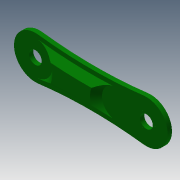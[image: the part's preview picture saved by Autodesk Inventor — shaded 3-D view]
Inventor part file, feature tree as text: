
AUTODESK INVENTOR PART (.ipt)
format: ipt  version: 2013 (Build 170138000, 138)  size: 299,008 bytes
history: native  units: mm
features: sketch x19, extrude x17, chamfer x1
ambient origin geometry x8: Origin, YZ Plane, XZ Plane, XY Plane, X Axis, Y Axis, Z Axis, Center Point
bodies: Solid1 (feature_tree)
feature tree (37):
  extrude  "Extrusion1"  Depth=50.0mm
  extrude  "Extrusion2"  Depth=6.0mm
  extrude  "Extrusion3"  Depth=5.0mm TaperAngle=0.0deg
  extrude  "Extrusion4"  Depth=20.0mm
  extrude  "Extrusion5"  Depth=20.0mm
  extrude  "Extrusion6"  Depth=3.0mm
  sketch  "Sketch7"  dims[d22=3.0mm d23=5.0mm d24=0.0mm]
  extrude  "Extrusion7"  Depth=5.0mm TaperAngle=0.0deg
  extrude  "Extrusion8"  Depth=1.0mm
  extrude  "Extrusion9"  Depth=1.0mm
  extrude  "Extrusion10"  Depth=15.0mm
  extrude  "Extrusion11"  Depth=5.0mm TaperAngle=0.0deg
  sketch  "Sketch12"  dims[d44=1.0mm d45=1.0mm]
  sketch  "Sketch13"  dims[d46=1.0mm d47=5.0mm d48=0.0mm]
  extrude  "Extrusion12"  Depth=1.0mm
  extrude  "Extrusion13"  Depth=5.0mm TaperAngle=0.0deg
  extrude  "Extrusion14"  Depth=5.0mm TaperAngle=0.0deg
  extrude  "Extrusion15"  Depth=5.0mm TaperAngle=0.0deg
  extrude  "Extrusion16"  Depth=43.308mm
  sketch  "Sketch18"  dims[d62=33.15mm]
  extrude  "Extrusion17"  Depth=20.0mm
  chamfer  "Chamfer1"  Distance=5.0mm
  sketch  "Sketch1"  dims[d0=150.0mm d1=50.0mm]
  sketch  "Sketch2"  dims[d2=5.0mm d3=0.0mm d4=6.0mm]
  sketch  "Sketch3"  dims[d5=6.0mm d6=5.0mm d7=0.0mm]
  sketch  "Sketch4"  dims[d11=55.0mm d12=20.0mm]
  sketch  "Sketch5"  dims[d13=40.2mm d14=20.0mm]
  sketch  "Sketch6"  dims[d20=3.0mm d21=3.0mm]
  sketch  "Sketch8"  dims[d32=5.0mm d33=0.0mm d34=1.0mm]
  sketch  "Sketch9"  dims[d35=1.0mm d36=1.0mm]
  sketch  "Sketch10"  dims[d37=5.0mm d38=0.0mm d39=15.0mm]
  sketch  "Sketch11"  dims[d40=15.0mm d41=5.0mm d42=0.0mm]
  sketch  "Sketch14"  dims[d49=5.0mm d50=0.0mm d51=5.0mm d52=0.0mm]
  sketch  "Sketch15"  dims[d53=130.0mm d54=5.0mm d55=0.0mm]
  sketch  "Sketch16"  dims[d56=15.0mm d57=43.308mm]
  sketch  "Sketch17"  dims[d58=40.2mm d59=20.0mm d60=5.0mm d61=0.0mm]
  sketch  "Sketch19"  dims[d63=18.1mm d64=55.0mm d65=40.2mm d66=20.0mm d67=5.0mm d68=0.0mm d69=33.15mm d70=18.1mm d71=55.0mm d72=40.2mm d73=20.0mm d74=5.0mm d75=0.0mm d76=5.0mm d77=0.0mm d84=5.0mm d85=0.0mm d86=5.0mm d87=0.0mm d95=7.0mm d96=0.0mm d97=7.0mm d98=2.0mm d99=45.0deg]
